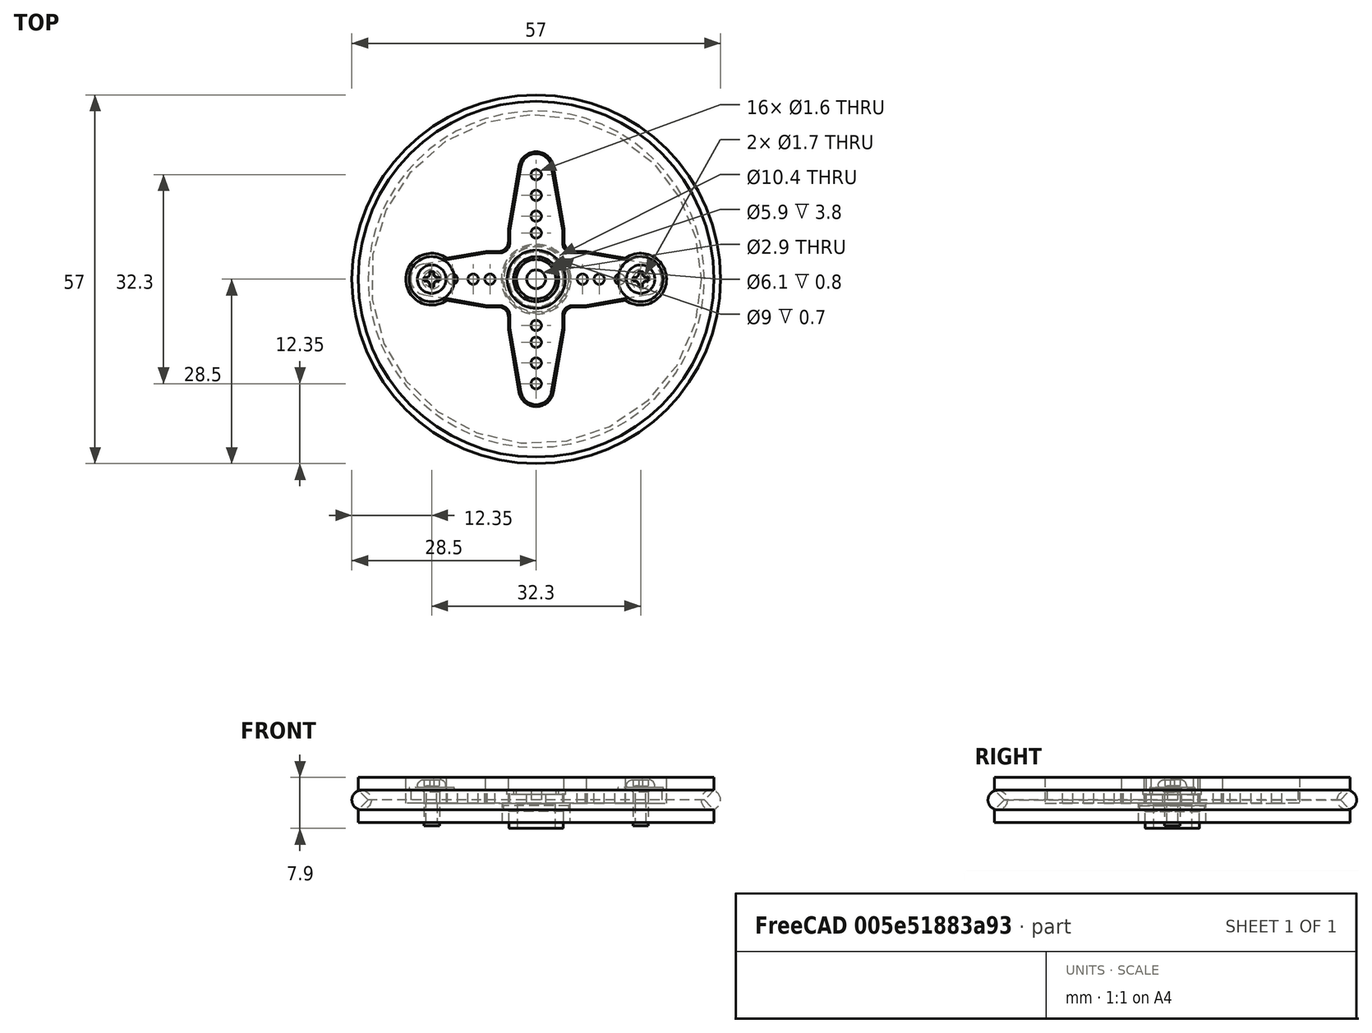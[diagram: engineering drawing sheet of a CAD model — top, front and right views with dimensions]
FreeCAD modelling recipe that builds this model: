
FCSTD DOCUMENT  (FreeCAD 0.14R3702 (Git))
Label: Renacuajo-wheel-4-arms-horn-assembly
License: CC-BY 3.0
LicenseURL: http://creativecommons.org/licenses/by/3.0/
objects: Part::Feature×4, Part::Torus×1, Part::Compound×1
note: 6 computed .brp shape members not serialized (recipe doc carries the construction recipe); baked Part::Feature solids carry a one-line shape summary decoded from their .brp

FEATURE [Part::Feature] PolarPattern  label="Renacuajo-wheel-4-arms-horn-final"
  shape: bbox 55 x 55 x 7 mm, 34 faces (baked)
FEATURE [Part::Feature] Fillet  label="4-arms-horn"
  Placement = pos=(0,0,-0.5) rot=(0,0,1;0rad)
  shape: bbox 38.8 x 38.8 x 6 mm, 58 faces (baked)
FEATURE [Part::Feature] Chamfer  label="screw002"
  Placement = pos=(-16.15,0,1.5) rot=(0,0,1;0rad)
  shape: bbox 7 x 7 x 7.14 mm, 33 faces (baked)
FEATURE [Part::Feature] Chamfer001  label="screw1"
  Placement = pos=(16.15,0,1.5) rot=(0,0,1;0rad)
  shape: bbox 7 x 7 x 7.14 mm, 33 faces (baked)
FEATURE [Part::Torus] Torus  label="o-ring"
  Angle1 = -180
  Angle2 = 180
  Angle3 = 360
  Radius1 = 27
  Radius2 = 1.5
FEATURE [Part::Compound] Compound  label="Renacuajo-wheel-4-arms-horn-assembly-final"
  Links = -> [PolarPattern,Fillet,Torus,Chamfer001,Chamfer]
